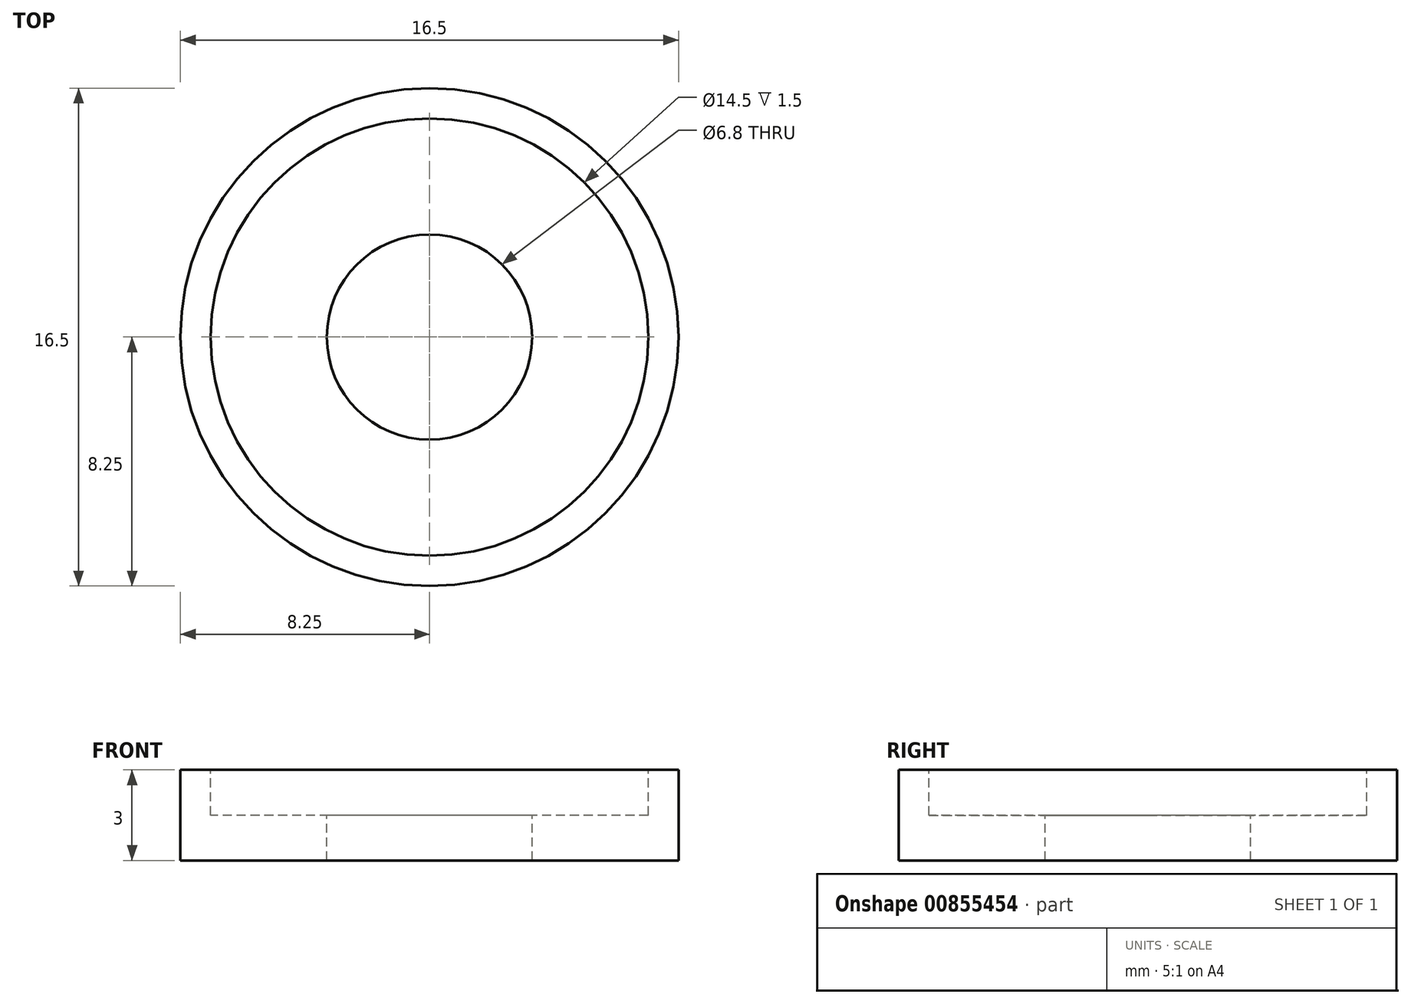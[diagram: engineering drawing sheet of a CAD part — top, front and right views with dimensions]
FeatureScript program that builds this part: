
annotation { "Feature Type Name" : "Feature", "Feature Type Description" : "" }
export const myFeature = defineFeature(function(context is Context, id is Id, definition is map)
    precondition{}
    {
        {
            var Q0;
            Q0=qCreatedBy(makeId("Front.planeOp"),FACE);
            var sketch = newSketch(context, id + "F0", { "sketchPlane" : qUnion([Q0])});
            skLineSegment(sketch, "E0", {"start": v(0, 0) * mm, "end": v(8.25, 0) * mm});
            skLineSegment(sketch, "E1", {"start": v(8.25, 0) * mm, "end": v(8.25, 3) * mm});
            skLineSegment(sketch, "E2", {"start": v(8.25, 3) * mm, "end": v(7.25, 3) * mm});
            skLineSegment(sketch, "E3", {"start": v(7.25, 3) * mm, "end": v(7.25, 1.5) * mm});
            skLineSegment(sketch, "E4", {"start": v(7.25, 1.5) * mm, "end": v(0, 1.5) * mm});
            skLineSegment(sketch, "E5", {"start": v(0, 1.5) * mm, "end": v(0, 0) * mm});
            skSolve(sketch);
        }
        {
            var Q0;
            Q0 = qSketchRegion(id + "F0", true);
            var Q1;
            Q1=sQuery(id+"F0.wireOp",EDGE,"E5");
            revolve(context, id + "F1", {"surfaceOperationType" : NewSurfaceOperationType.NEW, "entities" : qUnion([Q0]), "axis" : qUnion([Q1]), "revolveType" : RevolveType.FULL});
        }
        {
            var Q0;
            Q0=makeQuery(id+"F1.opRevolve","SWEPT_FACE",FACE,{"disambiguationData":[OSD([sQuery(id+"F0.wireOp",EDGE,"E4")])]});
            var sketch = newSketch(context, id + "F2", { "sketchPlane" : qUnion([Q0])});
            skCircle(sketch, "E6", {"center": v(0, 0) * mm, "radius": 3.4 * mm});
            skSolve(sketch);
        }
        {
            var Q0;
            Q0=makeQuery(id+"F2.imprint","IMPRINT",FACE,{"disambiguationData":[TD([[makeQuery(id+"F2.imprint","IMPRINT",EDGE,{"derivedFrom":sQuery(id+"F2.wireOp",EDGE,"E6")}),1.0]])]});
            extrude(context, id + "F3", {"entities" : qUnion([Q0]), "operationType" : NewBodyOperationType.REMOVE, "endBound" : BoundingType.THROUGH_ALL, "oppositeDirection" : true, "depth" : 25 * mm, "offsetDistance" : 25 * mm});
        }
    });
